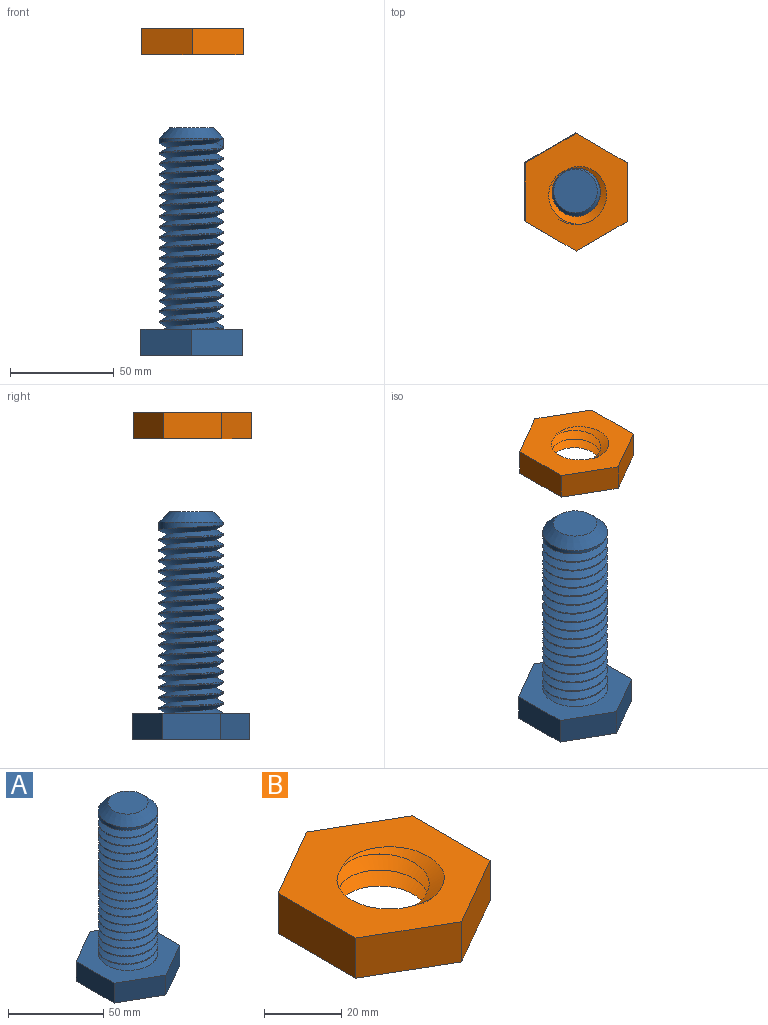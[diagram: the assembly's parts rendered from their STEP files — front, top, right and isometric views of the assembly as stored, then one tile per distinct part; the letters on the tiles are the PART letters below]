
ASSEMBLY  parts=2 mates=1
PART A: 16 faces, bbox 48.9x56.3x109.7 mm
  f0: cone r=10.52mm half-angle=45deg, axis (0,0,-1), area 589.4mm2, adj f9,f10,f11,f13
  f1: plane 28.17x12.7mm, normal (1,0,0), area 357.8mm2, adj f2,f6,f7,f8
  f2: plane 24.42x14.04mm, normal (0.5,0.87,0), area 357.8mm2, adj f1,f3,f7,f8
  f3: plane 24.37x14.13mm, normal (-0.5,0.87,0), area 357.8mm2, adj f2,f4,f7,f8
  f4: plane 28.17x12.7mm, normal (-1,0,0), area 357.8mm2, adj f3,f5,f7,f8
  f5: plane 24.42x14.04mm, normal (-0.5,-0.87,0), area 357.8mm2, adj f4,f6,f7,f8
  f6: plane 24.37x14.13mm, normal (0.5,-0.87,0), area 357.8mm2, adj f1,f5,f7,f8
  f7: plane 56.34x48.84mm, normal (0,0,1), area 1297.4mm2, adj f1,f2,f3,f4,f5,f6,f9,f15
  f8: plane 56.34x48.84mm, normal (0,0,-1), area 2061.8mm2, adj f1,f2,f3,f4,f5,f6
  f9: cylinder r=15.6mm len=91.95mm, axis (0,0,-1), area 2062.2mm2, adj f0,f7,f11,f12,f13,f14
  f10: plane 21.04x21.04mm, normal (0,0,1), area 347.6mm2, adj f0
  f11: plane 4.51x3.94mm, normal (0,-1,0), area 9mm2, adj f0,f9,f13,f14
  f12: plane 4.56x3.2mm, normal (0.59,0.81,0), area 9mm2, adj f9,f13,f14,f15
  f13: bspline ~94.56x36.02mm, area 7063mm2, adj f0,f9,f11,f12,f14
  f14: bspline ~94.56x36.02mm, area 7066mm2, adj f9,f11,f12,f13,f15
  f15: cylinder r=15.6mm len=31.2mm, axis (0,0,-1), area 190.5mm2, adj f7,f12,f14
PART B: 11 faces, bbox 49.1x56.7x18.4 mm
  f0: plane 56.7x49.11mm, normal (0,0,1), area 1482.3mm2, adj f2,f3,f4,f5,f6,f7,f8,f9
  f1: plane 56.7x49.11mm, normal (0,0,-1), area 1482.3mm2, adj f2,f3,f4,f5,f6,f7,f8,f9
  f2: plane 28.35x12.7mm, normal (1,0,0), area 360mm2, adj f0,f1,f3,f7
  f3: plane 24.55x14.19mm, normal (0.5,0.87,0), area 360mm2, adj f0,f1,f2,f4
  f4: plane 24.56x14.16mm, normal (-0.5,0.87,0), area 360mm2, adj f0,f1,f3,f5
  f5: plane 28.35x12.7mm, normal (-1,0,0), area 360mm2, adj f0,f1,f4,f6
  f6: plane 24.55x14.19mm, normal (-0.5,-0.87,0), area 360mm2, adj f0,f1,f5,f7
  f7: plane 24.56x14.16mm, normal (0.5,-0.87,0), area 360mm2, adj f0,f1,f2,f6
  f8: cylinder r=15.6mm len=31.2mm, axis (0,0,-1), area 129.2mm2, adj f0,f1,f9,f10
  f9: bspline ~36.02x31.2mm, area 976.4mm2, adj f0,f1,f8,f10
  f10: bspline ~36.02x31.2mm, area 976.4mm2, adj f0,f1,f8,f9
PLACE A t=(-53.53,-132.88,-151.83)mm
PLACE B t=(-53.2,-133.5,-32.47)mm
MATE cylindrical A.f0 <-> B.f0  axis (0,0,1) through (-53.53,-132.88,-42.1)mm
